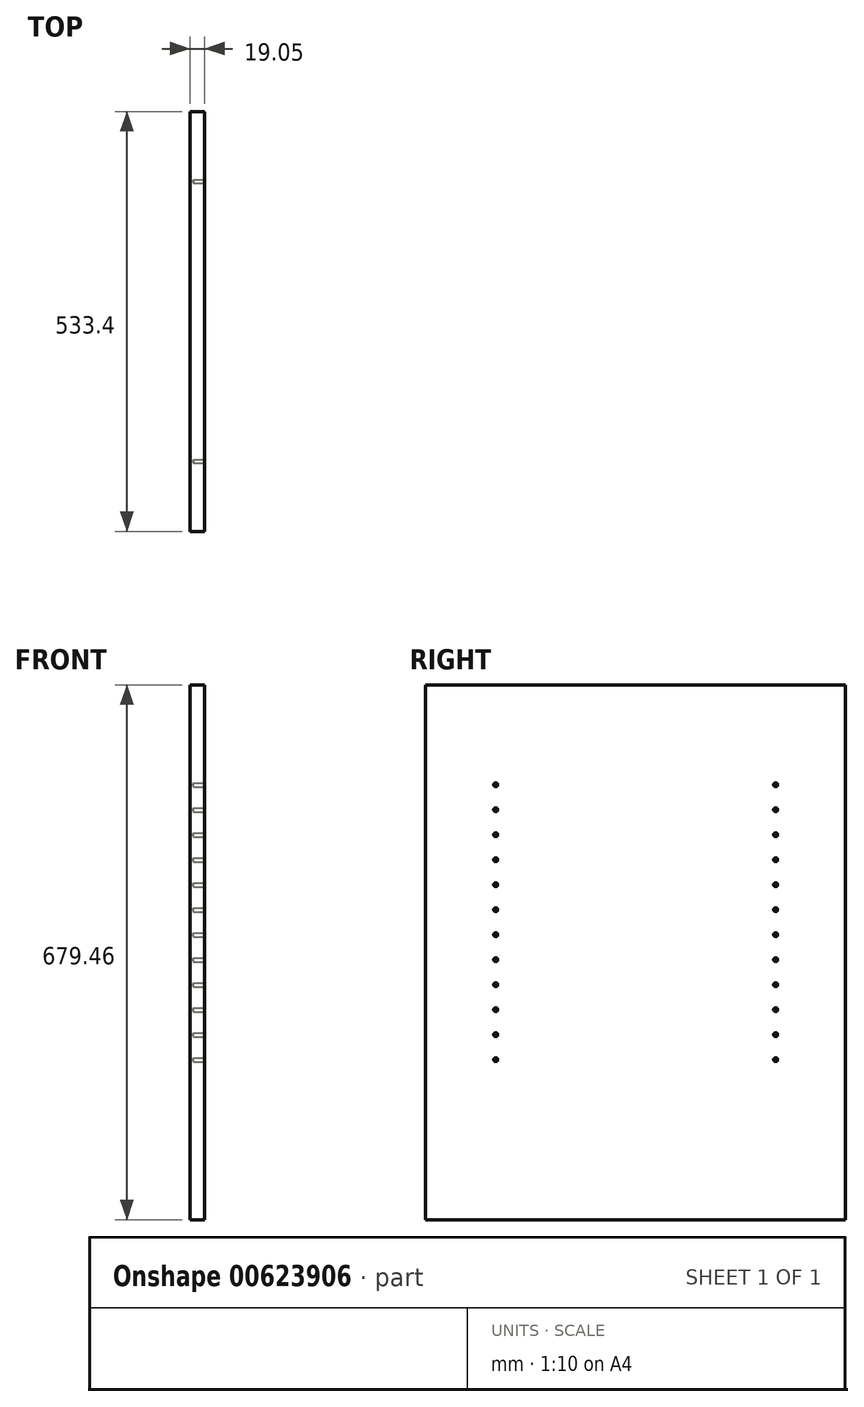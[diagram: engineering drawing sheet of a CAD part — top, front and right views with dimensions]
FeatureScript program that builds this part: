
annotation { "Feature Type Name" : "Feature", "Feature Type Description" : "" }
export const myFeature = defineFeature(function(context is Context, id is Id, definition is map)
    precondition{}
    {
        {
            var Q0;
            Q0=qCreatedBy(makeId("Right.planeOp"),FACE);
            var sketch = newSketch(context, id + "F0", { "sketchPlane" : qUnion([Q0])});
            skLineSegment(sketch, "E0.bottom", {"start": v(266.7, 339.73) * mm, "end": v(-266.7, 339.73) * mm});
            skLineSegment(sketch, "E0.top", {"start": v(266.7, -339.73) * mm, "end": v(-266.7, -339.73) * mm});
            skLineSegment(sketch, "E0.left", {"start": v(266.7, 339.72) * mm, "end": v(266.7, -339.73) * mm});
            skLineSegment(sketch, "E0.right", {"start": v(-266.7, 339.73) * mm, "end": v(-266.7, -339.73) * mm});
            skPoint(sketch, "E0.middle", {"position": v(0, 0) * mm});
            skSolve(sketch);
        }
        {
            var Q0;
            Q0=makeQuery(id+"F0.imprint","IMPRINT",FACE,{"disambiguationData":[TD([[makeQuery(id+"F0.imprint","IMPRINT",EDGE,{"derivedFrom":sQuery(id+"F0.wireOp",EDGE,"E0.bottom")}),1.0]])]});
            extrude(context, id + "F1", {"entities" : qUnion([Q0]), "depth" : 19.05 * mm, "offsetDistance" : 25.4 * mm});
        }
        {
            var Q0;
            Q0=makeQuery(id+"F1.opExtrude","CAP_FACE",FACE,{"disambiguationData":[OSD([sQuery(id+"F0.wireOp",EDGE,"E0.bottom"),sQuery(id+"F0.wireOp",EDGE,"E0.top"),sQuery(id+"F0.wireOp",EDGE,"E0.left"),sQuery(id+"F0.wireOp",EDGE,"E0.right")])],"isStart":false});
            var sketch = newSketch(context, id + "F2", { "sketchPlane" : qUnion([Q0])});
            skLineSegment(sketch, "E1", {"start": v(0, 339.73) * mm, "end": v(0, 180.97) * mm});
            skPoint(sketch, "E1.endSnap0", {"position": v(0, 339.73) * mm});
            skLineSegment(sketch, "E2.bottom", {"start": v(-177.8, 212.72) * mm, "end": v(177.8, 212.72) * mm});
            skLineSegment(sketch, "E2.top", {"start": v(-177.8, 149.22) * mm, "end": v(177.8, 149.22) * mm});
            skLineSegment(sketch, "E2.left", {"start": v(-177.8, 212.72) * mm, "end": v(-177.8, 149.22) * mm});
            skLineSegment(sketch, "E2.right", {"start": v(177.8, 212.72) * mm, "end": v(177.8, 149.22) * mm});
            skPoint(sketch, "E2.middle", {"position": v(0, 180.97) * mm});
            skLineSegment(sketch, "E3", {"start": v(0, 149.22) * mm, "end": v(0, 85.72) * mm});
            skPoint(sketch, "E3.endSnap0", {"position": v(0, 149.22) * mm});
            skLineSegment(sketch, "E4.bottom", {"start": v(-177.8, 53.97) * mm, "end": v(177.8, 53.97) * mm});
            skLineSegment(sketch, "E4.top", {"start": v(-177.8, 117.47) * mm, "end": v(177.8, 117.47) * mm});
            skLineSegment(sketch, "E4.left", {"start": v(-177.8, 53.97) * mm, "end": v(-177.8, 117.47) * mm});
            skLineSegment(sketch, "E4.right", {"start": v(177.8, 53.97) * mm, "end": v(177.8, 117.47) * mm});
            skPoint(sketch, "E4.middle", {"position": v(0, 85.72) * mm});
            skLineSegment(sketch, "E5", {"start": v(0, 53.97) * mm, "end": v(0, -9.53) * mm});
            skPoint(sketch, "E5.endSnap0", {"position": v(0, 53.97) * mm});
            skLineSegment(sketch, "E6.bottom", {"start": v(177.8, 22.22) * mm, "end": v(-177.8, 22.23) * mm});
            skLineSegment(sketch, "E6.top", {"start": v(177.8, -41.28) * mm, "end": v(-177.8, -41.27) * mm});
            skLineSegment(sketch, "E6.left", {"start": v(177.8, 22.22) * mm, "end": v(177.8, -41.28) * mm});
            skLineSegment(sketch, "E6.right", {"start": v(-177.8, 22.23) * mm, "end": v(-177.8, -41.27) * mm});
            skPoint(sketch, "E6.middle", {"position": v(0, -9.53) * mm});
            skLineSegment(sketch, "E7", {"start": v(0, -41.28) * mm, "end": v(0, -104.78) * mm});
            skPoint(sketch, "E7.endSnap0", {"position": v(0, -41.28) * mm});
            skLineSegment(sketch, "E8.bottom", {"start": v(-177.8, -73.03) * mm, "end": v(177.8, -73.03) * mm});
            skLineSegment(sketch, "E8.top", {"start": v(-177.8, -136.53) * mm, "end": v(177.8, -136.53) * mm});
            skLineSegment(sketch, "E8.left", {"start": v(-177.8, -73.03) * mm, "end": v(-177.8, -136.53) * mm});
            skLineSegment(sketch, "E8.right", {"start": v(177.8, -73.03) * mm, "end": v(177.8, -136.53) * mm});
            skPoint(sketch, "E8.middle", {"position": v(0, -104.78) * mm});
            skPoint(sketch, "E9", {"position": v(-177.8, 212.72) * mm});
            skPoint(sketch, "E10", {"position": v(-177.8, 180.97) * mm});
            skPoint(sketch, "E11", {"position": v(-177.8, 149.22) * mm});
            skPoint(sketch, "E12", {"position": v(-177.8, 117.47) * mm});
            skPoint(sketch, "E13", {"position": v(-177.8, 85.72) * mm});
            skPoint(sketch, "E14", {"position": v(-177.8, 53.97) * mm});
            skPoint(sketch, "E15", {"position": v(-177.8, 22.23) * mm});
            skPoint(sketch, "E16", {"position": v(-177.8, -9.52) * mm});
            skPoint(sketch, "E17", {"position": v(-177.8, -41.27) * mm});
            skPoint(sketch, "E18", {"position": v(-177.8, -73.03) * mm});
            skPoint(sketch, "E19", {"position": v(-177.8, -104.78) * mm});
            skPoint(sketch, "E20", {"position": v(-177.8, -136.53) * mm});
            skPoint(sketch, "E21", {"position": v(177.8, -136.53) * mm});
            skPoint(sketch, "E22", {"position": v(177.8, -104.78) * mm});
            skPoint(sketch, "E23", {"position": v(177.8, -73.03) * mm});
            skPoint(sketch, "E24", {"position": v(177.8, -41.28) * mm});
            skPoint(sketch, "E25", {"position": v(177.8, -9.53) * mm});
            skPoint(sketch, "E26", {"position": v(177.8, 22.22) * mm});
            skPoint(sketch, "E27", {"position": v(177.8, 53.97) * mm});
            skPoint(sketch, "E28", {"position": v(177.8, 85.72) * mm});
            skPoint(sketch, "E29", {"position": v(177.8, 117.47) * mm});
            skPoint(sketch, "E30", {"position": v(177.8, 149.22) * mm});
            skPoint(sketch, "E31", {"position": v(177.8, 180.97) * mm});
            skPoint(sketch, "E32", {"position": v(177.8, 212.72) * mm});
            skSolve(sketch);
        }
        {
            var Q0;
            Q0=sQuery(id+"F2.wireOp",VERTEX,"E9");
            var Q1;
            Q1=sQuery(id+"F2.wireOp",VERTEX,"E10");
            var Q2;
            Q2=sQuery(id+"F2.wireOp",VERTEX,"E11");
            var Q3;
            Q3=sQuery(id+"F2.wireOp",VERTEX,"E12");
            var Q4;
            Q4=sQuery(id+"F2.wireOp",VERTEX,"E13");
            var Q5;
            Q5=sQuery(id+"F2.wireOp",VERTEX,"E14");
            var Q6;
            Q6=sQuery(id+"F2.wireOp",VERTEX,"E15");
            var Q7;
            Q7=sQuery(id+"F2.wireOp",VERTEX,"E16");
            var Q8;
            Q8=sQuery(id+"F2.wireOp",VERTEX,"E17");
            var Q9;
            Q9=sQuery(id+"F2.wireOp",VERTEX,"E18");
            var Q10;
            Q10=sQuery(id+"F2.wireOp",VERTEX,"E19");
            var Q11;
            Q11=sQuery(id+"F2.wireOp",VERTEX,"E20");
            var Q12;
            Q12=sQuery(id+"F2.wireOp",VERTEX,"E21");
            var Q13;
            Q13=sQuery(id+"F2.wireOp",VERTEX,"E22");
            var Q14;
            Q14=sQuery(id+"F2.wireOp",VERTEX,"E23");
            var Q15;
            Q15=sQuery(id+"F2.wireOp",VERTEX,"E24");
            var Q16;
            Q16=sQuery(id+"F2.wireOp",VERTEX,"E25");
            var Q17;
            Q17=sQuery(id+"F2.wireOp",VERTEX,"E26");
            var Q18;
            Q18=sQuery(id+"F2.wireOp",VERTEX,"E27");
            var Q19;
            Q19=sQuery(id+"F2.wireOp",VERTEX,"E28");
            var Q20;
            Q20=sQuery(id+"F2.wireOp",VERTEX,"E29");
            var Q21;
            Q21=sQuery(id+"F2.wireOp",VERTEX,"E30");
            var Q22;
            Q22=sQuery(id+"F2.wireOp",VERTEX,"E31");
            var Q23;
            Q23=sQuery(id+"F2.wireOp",VERTEX,"E32");
            var Q24;
            Q24=makeQuery(id+"F1.opExtrude","SWEPT_BODY",BODY,{"disambiguationData":[OSD([sQuery(id+"F0.wireOp",EDGE,"E0.bottom"),sQuery(id+"F0.wireOp",EDGE,"E0.top"),sQuery(id+"F0.wireOp",EDGE,"E0.left"),sQuery(id+"F0.wireOp",EDGE,"E0.right")])]});
            hole(context, id + "F3", {"style" : HoleStyle.SIMPLE, "endStyle" : HoleEndStyle.BLIND, "holeDiameter" : 5 * mm, "majorDiameter" : 6.35 * mm, "holeDepth" : 14.22 * mm, "isTappedThrough" : true, "tappedDepth" : 12.7 * mm, "tapClearance" : 3, "startFromSketch" : true, "locations" : qUnion([Q0, Q1, Q2, Q3, Q4, Q5, Q6, Q7, Q8, Q9, Q10, Q11, Q12, Q13, Q14, Q15, Q16, Q17, Q18, Q19, Q20, Q21, Q22, Q23]), "scope" : qUnion([Q24])});
        }
    });
